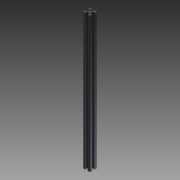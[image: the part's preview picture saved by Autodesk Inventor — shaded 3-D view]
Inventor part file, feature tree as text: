
AUTODESK INVENTOR PART (.ipt)
format: ipt  version: 2011 SP1 (Build 150282100, 282)  size: 159,744 bytes
history: native  units: mm
features: other x7, sketch x2, extrude x1, revolve x1
ambient origin geometry x8: Origin, YZ Plane, XZ Plane, XY Plane, X Axis, Y Axis, Z Axis, Center Point
bodies: Solid1 (feature_tree)
feature tree (11):
  extrude  "Extrusion1"  TaperAngle=360.0deg  [1 undecoded]
  revolve  "Revolution1"  [1 undecoded]
  other  "C1_XY"
  other  "C1_YZ"
  other  "C1_ZX"
  other  "C1_X"
  other  "C1_Y"
  other  "C1_Z"
  other  "C1_Center"
  sketch  "Sketch_1"  dims[d0=400.0mm d1=0.0mm d2=360.0deg]
  sketch  "Sketch_2"
note: 2 required parameter values undecoded (feature->parameter linkage not recoverable at this tier; creation-order binding heuristic only, values carry confidence <= 0.55)
